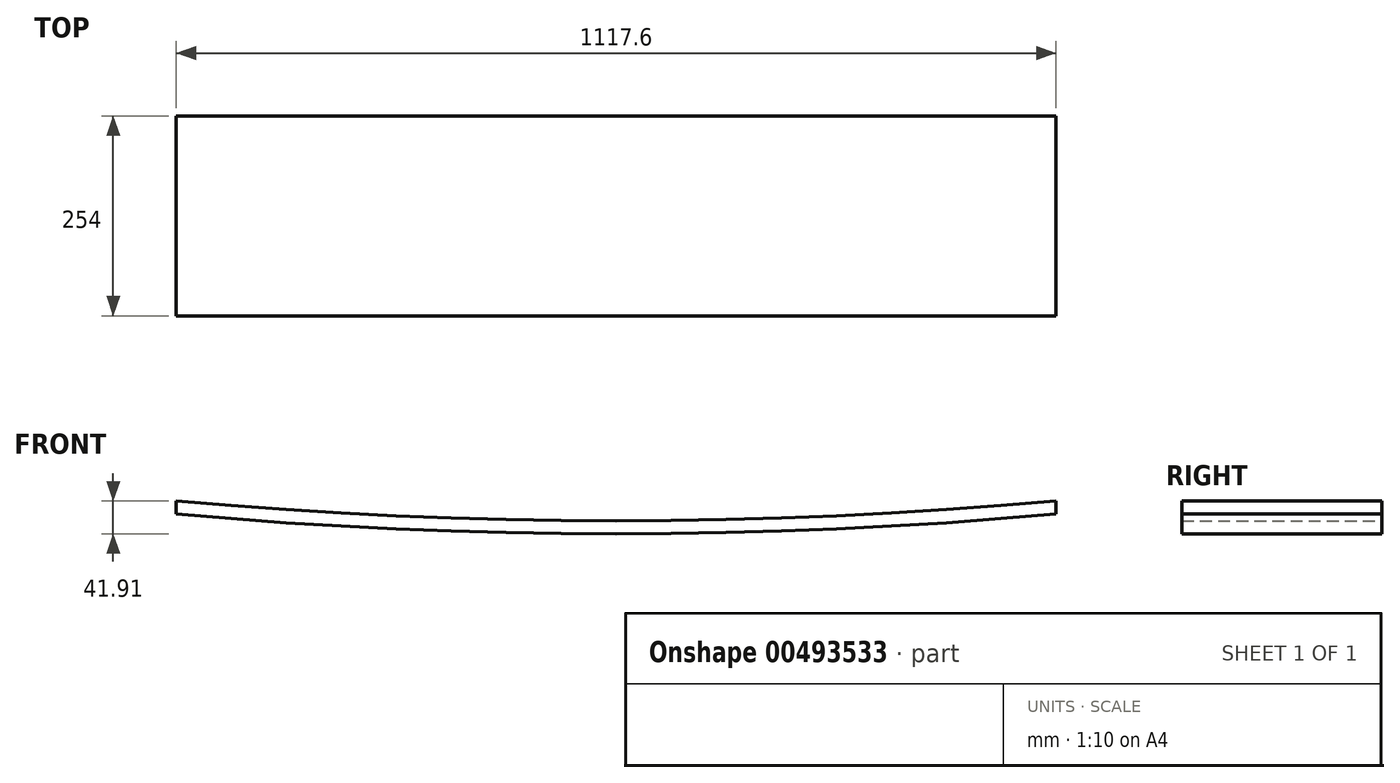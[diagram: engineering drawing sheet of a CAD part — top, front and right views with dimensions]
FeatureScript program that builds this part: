
annotation { "Feature Type Name" : "Feature", "Feature Type Description" : "" }
export const myFeature = defineFeature(function(context is Context, id is Id, definition is map)
    precondition{}
    {
        {
            var Q0;
            Q0=qCreatedBy(makeId("Front.planeOp"),FACE);
            var sketch = newSketch(context, id + "F0", { "sketchPlane" : qUnion([Q0])});
            skLineSegment(sketch, "E0", {"start": v(0, 0) * mm, "end": v(1117.6, 0) * mm, "construction": true});
            skLineSegment(sketch, "E1", {"start": v(558.8, 0) * mm, "end": v(558.8, -25.4) * mm, "construction": true});
            skArc(sketch, "E2", {"start": v(0, 0) * mm, "mid": v(558.8, -25.4) * mm, "end": v(1117.6, 0) * mm});
            skArc(sketch, "E3.0", {"start": v(0, -16.58) * mm, "mid": v(558.8, -41.9) * mm, "end": v(1117.6, -16.58) * mm});
            skLineSegment(sketch, "E4", {"start": v(1117.6, 0) * mm, "end": v(1117.6, -16.58) * mm});
            skLineSegment(sketch, "E5", {"start": v(0, 0) * mm, "end": v(0, -16.58) * mm});
            skSolve(sketch);
        }
        {
            var Q0;
            Q0 = qSketchRegion(id + "F0", true);
            extrude(context, id + "F1", {"entities" : qUnion([Q0]), "depth" : 254 * mm, "offsetDistance" : 25.4 * mm});
        }
    });
